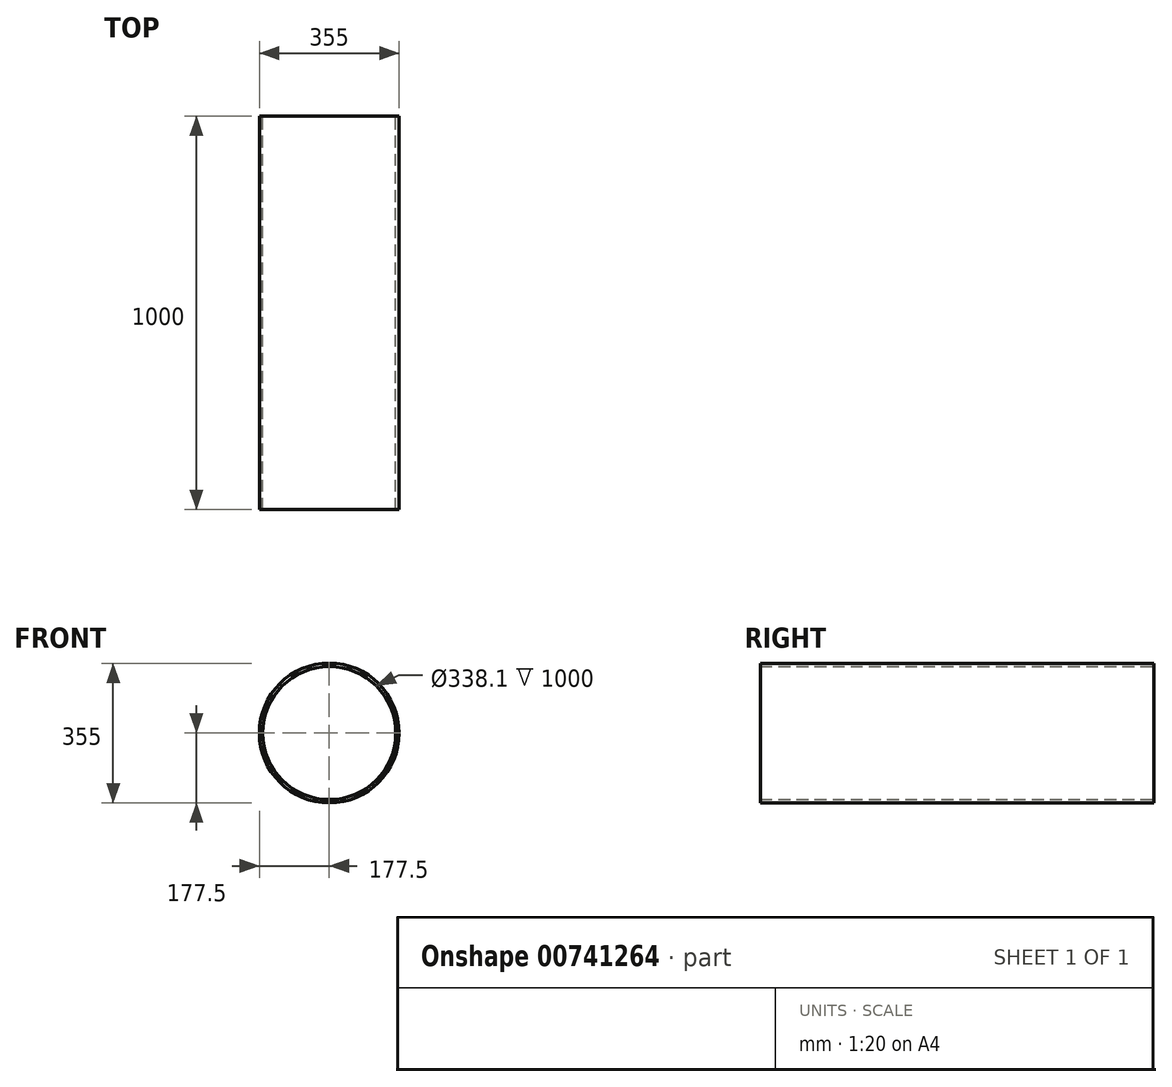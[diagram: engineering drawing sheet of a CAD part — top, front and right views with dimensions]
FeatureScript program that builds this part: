
annotation { "Feature Type Name" : "Feature", "Feature Type Description" : "" }
export const myFeature = defineFeature(function(context is Context, id is Id, definition is map)
    precondition{}
    {
        {
            var Q0;
            Q0=qCreatedBy(makeId("Front.planeOp"),FACE);
            var sketch = newSketch(context, id + "F0", { "sketchPlane" : qUnion([Q0])});
            skCircle(sketch, "E0", {"center": v(0, 0) * mm, "radius": 177.5 * mm});
            skCircle(sketch, "E1", {"center": v(0, 0) * mm, "radius": 169.05 * mm});
            skSolve(sketch);
        }
        {
            var Q0;
            Q0=makeQuery(id+"F0.imprint","IMPRINT",FACE,{"disambiguationData":[TD([[makeQuery(id+"F0.imprint","IMPRINT",EDGE,{"derivedFrom":sQuery(id+"F0.wireOp",EDGE,"E0")}),1.0]])]});
            extrude(context, id + "F1", {"entities" : qUnion([Q0]), "endBound" : BoundingType.SYMMETRIC, "depth" : 1000 * mm, "offsetDistance" : 25 * mm});
        }
    });
